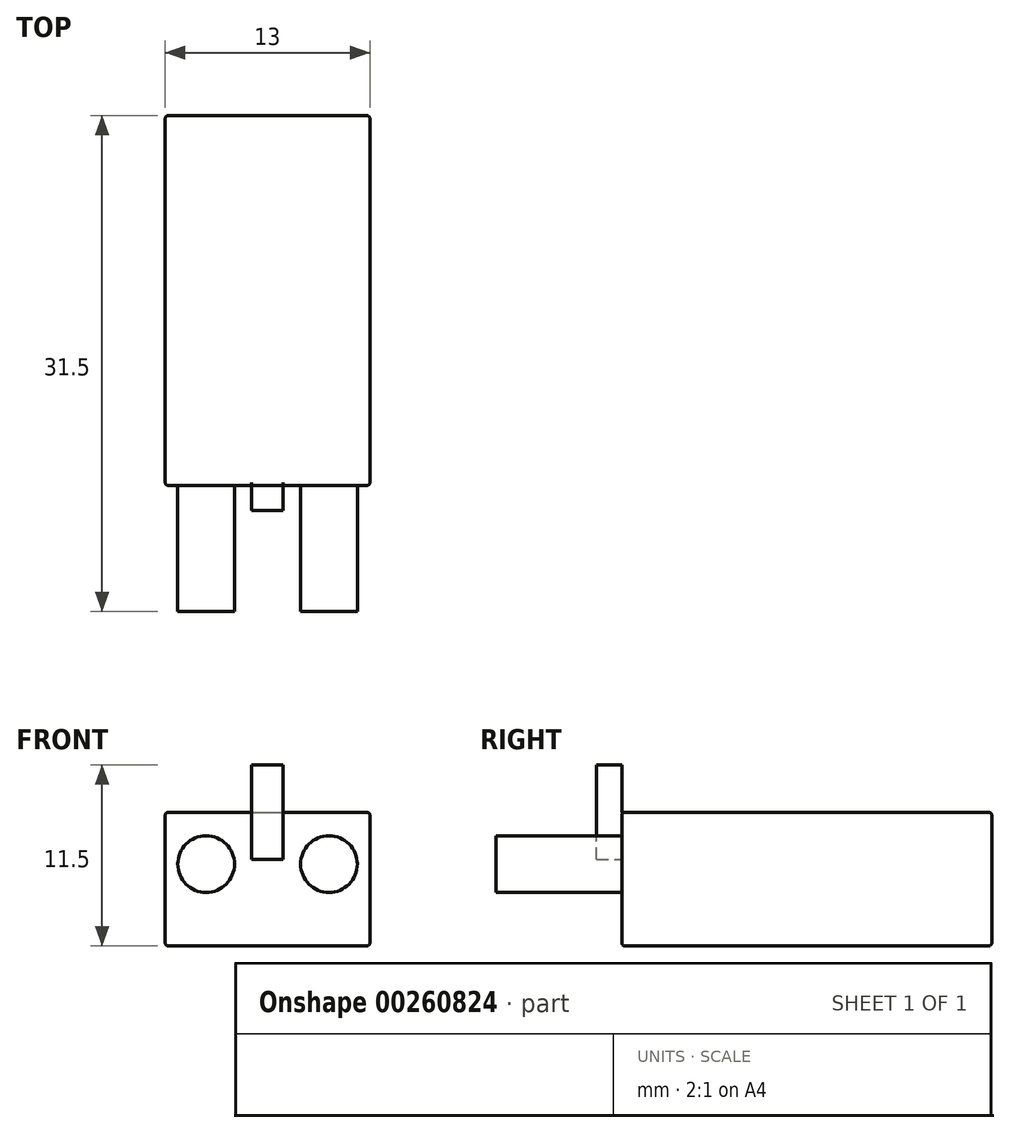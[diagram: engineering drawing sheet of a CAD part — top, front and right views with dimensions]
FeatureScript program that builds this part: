
annotation { "Feature Type Name" : "Feature", "Feature Type Description" : "" }
export const myFeature = defineFeature(function(context is Context, id is Id, definition is map)
    precondition{}
    {
        {
            var Q0;
            Q0=qCreatedBy(makeId("Top.planeOp"),FACE);
            var sketch = newSketch(context, id + "F0", { "sketchPlane" : qUnion([Q0])});
            skLineSegment(sketch, "E0.bottom", {"start": v(0, 0) * mm, "end": v(13, 0) * mm});
            skLineSegment(sketch, "E0.top", {"start": v(0, 23.5) * mm, "end": v(13, 23.5) * mm});
            skLineSegment(sketch, "E0.left", {"start": v(0, 0) * mm, "end": v(0, 23.5) * mm});
            skLineSegment(sketch, "E0.right", {"start": v(13, 0) * mm, "end": v(13, 23.5) * mm});
            skSolve(sketch);
        }
        {
            var Q0;
            Q0 = qSketchRegion(id + "F0", true);
            extrude(context, id + "F1", {"entities" : qUnion([Q0]), "depth" : 8.5 * mm});
        }
        {
            var Q0;
            Q0=makeQuery(id+"F1.opExtrude","SWEPT_FACE",FACE,{"disambiguationData":[OSD([sQuery(id+"F0.wireOp",EDGE,"E0.bottom")])]});
            var sketch = newSketch(context, id + "F2", { "sketchPlane" : qUnion([Q0])});
            skCircle(sketch, "E1", {"center": v(2.6, 5.2) * mm, "radius": 1.8 * mm});
            skCircle(sketch, "E2", {"center": v(10.4, 5.2) * mm, "radius": 1.8 * mm});
            skSolve(sketch);
        }
        {
            var Q0;
            Q0 = qSketchRegion(id + "F2", true);
            extrude(context, id + "F3", {"entities" : qUnion([Q0]), "operationType" : NewBodyOperationType.ADD, "depth" : 8 * mm});
        }
        {
            var Q0;
            Q0=makeQuery(id+"F1.opExtrude","SWEPT_FACE",FACE,{"disambiguationData":[OSD([sQuery(id+"F0.wireOp",EDGE,"E0.bottom")])]});
            var sketch = newSketch(context, id + "F4", { "sketchPlane" : qUnion([Q0])});
            skLineSegment(sketch, "E3.bottom", {"start": v(7.5, 5.5) * mm, "end": v(5.5, 5.5) * mm});
            skLineSegment(sketch, "E3.top", {"start": v(7.5, 11.5) * mm, "end": v(5.5, 11.5) * mm});
            skLineSegment(sketch, "E3.left", {"start": v(7.5, 5.5) * mm, "end": v(7.5, 11.5) * mm});
            skLineSegment(sketch, "E3.right", {"start": v(5.5, 5.5) * mm, "end": v(5.5, 11.5) * mm});
            skPoint(sketch, "E3.middle", {"position": v(6.5, 8.5) * mm});
            skSolve(sketch);
        }
        {
            var Q0;
            Q0 = qSketchRegion(id + "F4", true);
            extrude(context, id + "F5", {"entities" : qUnion([Q0]), "operationType" : NewBodyOperationType.ADD, "depth" : 1.6 * mm});
        }
        {
            var Q0;
            Q0=makeQuery(id+"F1.opExtrude","CAP_EDGE",EDGE,{"disambiguationData":[OSD([sQuery(id+"F0.wireOp",EDGE,"E0.top")])],"isStart":true});
            var Q1;
            Q1=makeQuery(id+"F1.opExtrude","CAP_EDGE",EDGE,{"disambiguationData":[OSD([sQuery(id+"F0.wireOp",EDGE,"E0.right")])],"isStart":true});
            var Q2;
            Q2=makeQuery(id+"F1.opExtrude","CAP_EDGE",EDGE,{"disambiguationData":[OSD([sQuery(id+"F0.wireOp",EDGE,"E0.left")])],"isStart":true});
            var Q3;
            Q3=makeQuery(id+"F1.opExtrude","SWEPT_EDGE",EDGE,{"disambiguationData":[OSD([sQuery(id+"F0.wireOp",EDGE,"E0.top"),sQuery(id+"F0.wireOp",EDGE,"E0.right")])]});
            var Q4;
            Q4=makeQuery(id+"F1.opExtrude","CAP_EDGE",EDGE,{"disambiguationData":[OSD([sQuery(id+"F0.wireOp",EDGE,"E0.right")])],"isStart":false});
            var Q5;
            Q5=makeQuery(id+"F1.opExtrude","CAP_EDGE",EDGE,{"disambiguationData":[OSD([sQuery(id+"F0.wireOp",EDGE,"E0.top")])],"isStart":false});
            var Q6;
            Q6=makeQuery(id+"F1.opExtrude","CAP_EDGE",EDGE,{"disambiguationData":[OSD([sQuery(id+"F0.wireOp",EDGE,"E0.left")])],"isStart":false});
            var Q7;
            Q7=makeQuery(id+"F1.opExtrude","SWEPT_EDGE",EDGE,{"disambiguationData":[OSD([sQuery(id+"F0.wireOp",EDGE,"E0.top"),sQuery(id+"F0.wireOp",EDGE,"E0.left")])]});
            var Q8;
            Q8=makeQuery(id+"F1.opExtrude","SWEPT_FACE",FACE,{"disambiguationData":[OSD([sQuery(id+"F0.wireOp",EDGE,"E0.left")])]});
            var Q9;
            {var subQ0=sQuery(id+"F4.wireOp",EDGE,"E3.right");var subQ1=sQuery(id+"F0.wireOp",EDGE,"E0.left");var subQ2=sQuery(id+"F0.wireOp",EDGE,"E0.bottom");Q9=makeQuery(id+"F5.boolean.opBoolean","SPLIT",EDGE,{"disambiguationData":[TD([makeQuery(id+"F1.opExtrude","SWEPT_FACE",FACE,{"disambiguationData":[OSD([subQ2])]}),makeQuery(id+"F1.opExtrude","CAP_FACE",FACE,{"disambiguationData":[OSD([subQ2,sQuery(id+"F0.wireOp",EDGE,"E0.top"),subQ1,sQuery(id+"F0.wireOp",EDGE,"E0.right")])],"isStart":false}),makeQuery(id+"F1.opExtrude","SWEPT_FACE",FACE,{"disambiguationData":[OSD([subQ1])]}),makeQuery(id+"F5.opExtrude","CAP_FACE",FACE,{"disambiguationData":[OSD([sQuery(id+"F4.wireOp",EDGE,"E3.bottom"),sQuery(id+"F4.wireOp",EDGE,"E3.top"),sQuery(id+"F4.wireOp",EDGE,"E3.left"),subQ0])],"isStart":true}),makeQuery(id+"F5.opExtrude","SWEPT_FACE",FACE,{"disambiguationData":[OSD([subQ0])]})])],"derivedFrom":makeQuery(id+"F1.opExtrude","CAP_EDGE",EDGE,{"disambiguationData":[OSD([subQ2])],"isStart":false})});}
            var Q10;
            {var subQ0=sQuery(id+"F4.wireOp",EDGE,"E3.left");var subQ1=sQuery(id+"F0.wireOp",EDGE,"E0.right");var subQ2=sQuery(id+"F0.wireOp",EDGE,"E0.bottom");Q10=makeQuery(id+"F5.boolean.opBoolean","SPLIT",EDGE,{"disambiguationData":[TD([makeQuery(id+"F1.opExtrude","SWEPT_FACE",FACE,{"disambiguationData":[OSD([subQ2])]}),makeQuery(id+"F1.opExtrude","CAP_FACE",FACE,{"disambiguationData":[OSD([subQ2,sQuery(id+"F0.wireOp",EDGE,"E0.top"),sQuery(id+"F0.wireOp",EDGE,"E0.left"),subQ1])],"isStart":false}),makeQuery(id+"F1.opExtrude","SWEPT_FACE",FACE,{"disambiguationData":[OSD([subQ1])]}),makeQuery(id+"F5.opExtrude","CAP_FACE",FACE,{"disambiguationData":[OSD([sQuery(id+"F4.wireOp",EDGE,"E3.bottom"),sQuery(id+"F4.wireOp",EDGE,"E3.top"),subQ0,sQuery(id+"F4.wireOp",EDGE,"E3.right")])],"isStart":true}),makeQuery(id+"F5.opExtrude","SWEPT_FACE",FACE,{"disambiguationData":[OSD([subQ0])]})])],"derivedFrom":makeQuery(id+"F1.opExtrude","CAP_EDGE",EDGE,{"disambiguationData":[OSD([subQ2])],"isStart":false})});}
            var Q11;
            Q11=makeQuery(id+"F1.opExtrude","SWEPT_FACE",FACE,{"disambiguationData":[OSD([sQuery(id+"F0.wireOp",EDGE,"E0.right")])]});
            var Q12;
            Q12=makeQuery(id+"F1.opExtrude","CAP_EDGE",EDGE,{"disambiguationData":[OSD([sQuery(id+"F0.wireOp",EDGE,"E0.bottom")])],"isStart":true});
            fillet(context, id + "F6", {"entities" : qUnion([Q0, Q1, Q2, Q3, Q4, Q5, Q6, Q7, Q8, Q9, Q10, Q11, Q12]), "radius" : 0.2 * mm, "tangentPropagation" : true, "allowEdgeOverflow" : false});
        }
    });
